# Revit family: 0068188
name_source: partatom
category: Lighting Fixtures
revit_build: Autodesk Revit 2017 (Build: 20190507_1515(x64)
units: mm (PartAtom-declared; Revit-internal decimal feet)

## family parameters
Cut with Voids When Loaded = No
Host = Face
Light Source = Yes
OmniClass Number = 23.80.70.00
OmniClass Title = Lighting
Part Type = Normal
Room Calculation Point = No
Round Connector Dimension = Use Diameter
Shared = No

## types (4) — shared parameters
Apparent Load = 72 VA
Assembly Code = D5020200
AssetType = Fixed
CABLE_BLEND_SYL = 12 mm  [stored 0.0393701 ft]
CABLE_DIST2_SYL = 2 mm  [stored 0.00656168 ft]
CABLE_DIST_SYL = 2 mm  [stored 0.00656168 ft]
CABLE_END_SYL = 15 mm  [stored 0.0492126 ft]
CABLE_FIX_SYL = 1 mm  [stored 0.00328084 ft]
CABLE_LENGHT_SYL = 1000 mm  [stored 3.28084 ft]
ClassificationName = Uniclass2015
ClassificationValue = EF_70_80
Color Filter = 16777215
Default Elevation = 1219 mm
Dimming Lamp Color Temperature Shift = <None>
DocumentationLiterature = http://www.sylvania-lighting.com
ElectricShockClassification = Class III
Emit Shape Visible in Rendering = No
Emit from Circle Diameter = 610 mm
IfcExportAs = IfcLightFixtureType
IfcExportType = IfcLightFixtureType
ImpactProtectionIndex = IK00
IngressProtection = IP65
Keynote = 16500
LED_CH_L_DEPTH_SYL = 1 mm  [stored 0.00328084 ft]
LED_CH_L_DIST1_SYL = 52 mm
LED_CH_L_DIST_SYL = 13 mm
LED_CH_L_WIDTH_SYL = 2 mm  [stored 0.00656168 ft]
LED_CH_S_DEPTH1_SYL = 1 mm  [stored 0.00328084 ft]
LED_CH_S_DEPTH2_SYL = 1 mm  [stored 0.00328084 ft]
LED_CH_S_WIDTH_SYL = 2 mm  [stored 0.00656168 ft]
LUM_LENGHT_SYL = 5000 mm  [stored 16.4042 ft]
LUM_LENGHT_SYL!!!! = MUST BE DIVISIBLE WITH 100
LUM_WIDTH_SYL = 5 mm  [stored 0.0164042 ft]
Lamp = LED
LampColourRenderingIndex = 90
LampsType = LED
Manufacturer = Feilo Sylvania
ManufacturerName = Feilo Sylvania
Material = other housing
Material_1_SYL = Default
Material_2_SYL = Default New Material(1)
Material_3_SYL = Default New Material
Material_4_SYL = <By Category>
NominalDepth = 12 mm  [stored 0.0393701 ft]
NominalHeight = 4 mm  [stored 0.0131234 ft]
NominalLength = 5000 mm  [stored 16.4042 ft]
PHOTOMETRY1_SYL = 2500 mm  [stored 8.2021 ft]
PHOTOMETRY2_SYL = 5 mm  [stored 0.0164042 ft]
PowerConsumption = 72 W
Tilt Angle = -90.00°
Type Image = <None>
URL = http://www.sylvania-lighting.com
Voltage = 0 V
Weight = 4.0 kg
zero-valued in all types: Cost, PHOTOMETRY3_SYL, PowerFactor

## per-type parameters (varying)
| type | LampColourTemperature | LampNominalLuminous | LuminousEfficacy | Model | ModelNumber | ModelReference | Name | Photometric Web File | TypeName |
| 0068189 FLEX PRO IP65 8900LM 940 | 4000 K | 8900 lm | 122 lm/W | Flex Pro IP65 8900lm 940 | 0068189 | Flex Pro IP65 8900lm 940 | Flex Pro IP65 8900lm 940 | 0068189.ies | Flex Pro IP65 8900lm 940 |
| 0068188 FLEX PRO IP65 8250LM 930 | 3000 K | 8250 lm | 113 lm/W | Flex Pro IP65 8250lm 930 | 0068188 | Flex Pro IP65 8250lm 930 | Flex Pro IP65 8250lm 930 | 0068188.ies | Flex Pro IP65 8250lm 930 |
| 0068187 FLEX PRO IP65 7600LM 927 | 2700 K | 7600 lm | 104 lm/W | Flex Pro IP65 7600lm 927 | 0068187 | Flex Pro IP65 7600lm 927 | Flex Pro IP65 7600lm 927 | 0068187.ies | Flex Pro IP65 7600lm 927 |
| 0068190 FLEX PRO IP65 8750LM 965 | 6500 K | 8750 lm | 120 lm/W | Flex Pro IP65 8750lm 965 | 0068190 | Flex Pro IP65 8750lm 965 | Flex Pro IP65 8750lm 965 | 0068190.ies | Flex Pro IP65 8750lm 965 |

note: [stored X ft] marks values corroborated as IEEE doubles in the binary element streams (Revit-internal decimal feet)

## geometry (parser evidence)
native form markers: Sweep x1
no freeform markers — native parametric forms only
